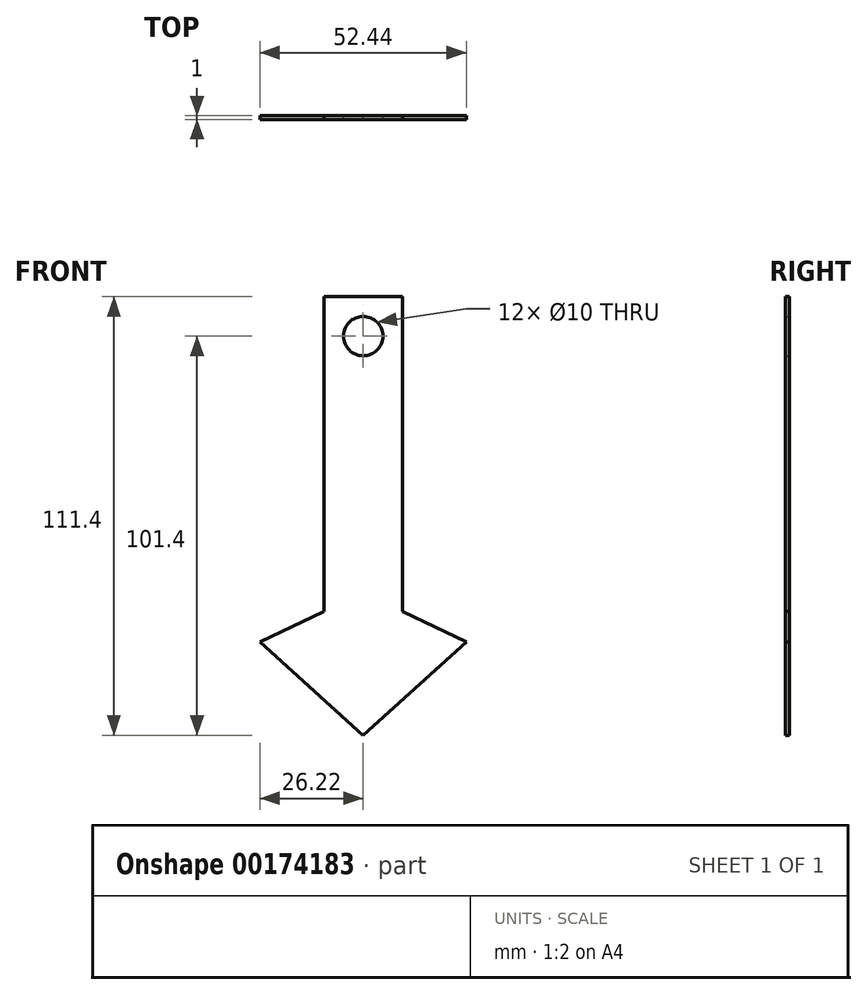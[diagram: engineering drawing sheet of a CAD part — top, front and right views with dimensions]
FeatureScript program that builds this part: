
annotation { "Feature Type Name" : "Feature", "Feature Type Description" : "" }
export const myFeature = defineFeature(function(context is Context, id is Id, definition is map)
    precondition{}
    {
        {
            var Q0;
            Q0=qCreatedBy(makeId("Front.planeOp"),FACE);
            var sketch = newSketch(context, id + "F0", { "sketchPlane" : qUnion([Q0])});
            skLineSegment(sketch, "E0.bottom", {"start": v(-10, 10) * mm, "end": v(10, 10) * mm});
            skLineSegment(sketch, "E0.top", {"start": v(-10, -70) * mm, "end": v(10, -70) * mm});
            skLineSegment(sketch, "E0.left", {"start": v(-10, 10) * mm, "end": v(-10, -70) * mm});
            skLineSegment(sketch, "E0.right", {"start": v(10, 10) * mm, "end": v(10, -70) * mm});
            skLineSegment(sketch, "E1", {"start": v(-26.22, -77.66) * mm, "end": v(0, -101.4) * mm});
            skLineSegment(sketch, "E2", {"start": v(-26.22, -77.66) * mm, "end": v(-10, -70) * mm});
            skLineSegment(sketch, "E3", {"start": v(0, -74.8) * mm, "end": v(0, -34.4) * mm, "construction": true});
            skLineSegment(sketch, "E4.MirrorCS", {"start": v(26.22, -77.66) * mm, "end": v(10, -70) * mm});
            skLineSegment(sketch, "E5.MirrorCS", {"start": v(26.22, -77.66) * mm, "end": v(0, -101.4) * mm});
            skCircle(sketch, "E6", {"center": v(0, 0) * mm, "radius": 5 * mm});
            skSolve(sketch);
        }
        {
            var Q0;
            Q0=makeQuery(id+"F0.imprint","IMPRINT",FACE,{"disambiguationData":[TD([[makeQuery(id+"F0.imprint","IMPRINT",EDGE,{"derivedFrom":sQuery(id+"F0.wireOp",EDGE,"E0.bottom")}),-1.0]])]});
            var Q1;
            Q1=makeQuery(id+"F0.imprint","IMPRINT",FACE,{"disambiguationData":[TD([[makeQuery(id+"F0.imprint","IMPRINT",EDGE,{"derivedFrom":sQuery(id+"F0.wireOp",EDGE,"E0.top")}),-1.0]])]});
            extrude(context, id + "F1", {"entities" : qUnion([Q0, Q1]), "depth" : 1 * mm});
        }
    });
